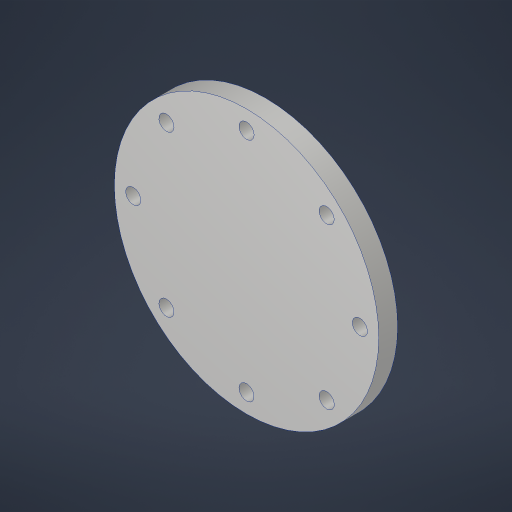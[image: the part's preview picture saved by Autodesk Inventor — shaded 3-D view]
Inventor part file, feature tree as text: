
AUTODESK INVENTOR PART (.ipt)
format: ipt  version: 2023.4 (Build 274418000, 418)  size: 185,856 bytes
history: native  units: in
note: dims shown in document units (in); Inventor stores cm internally (conversion verified against a paired STEP export)
features: sketch x2, extrude x1, hole x1, pattern_circular x1, projected_geometry x1
ambient origin geometry x8: Origin, YZ Plane, XZ Plane, XY Plane, X Axis, Y Axis, Z Axis, Center Point
bodies: Solid1 (feature_tree)
feature tree (6):
  extrude  "Extrusion1"  Depth=0.25in TaperAngle=0.0deg
  hole  "Hole1"  [1 undecoded]
  pattern_circular  "Circular Pattern1"  [2 undecoded]
  sketch  "Sketch1"  dims[d0=3.5in d1=0.25in d2=0.0in]
  sketch  "Sketch2"  dims[d3=3.0in d4=0.201in d5=0.75in d6=0.385in d7=0.25in d8=0.5635in d9=1.0in d10=0.8108in d11=3.1496in d12=360.0deg]
  projected_geometry  "Project Cut Edges1"
note: 3 required parameter values undecoded (feature->parameter linkage not recoverable at this tier; creation-order binding heuristic only, values carry confidence <= 0.55)
